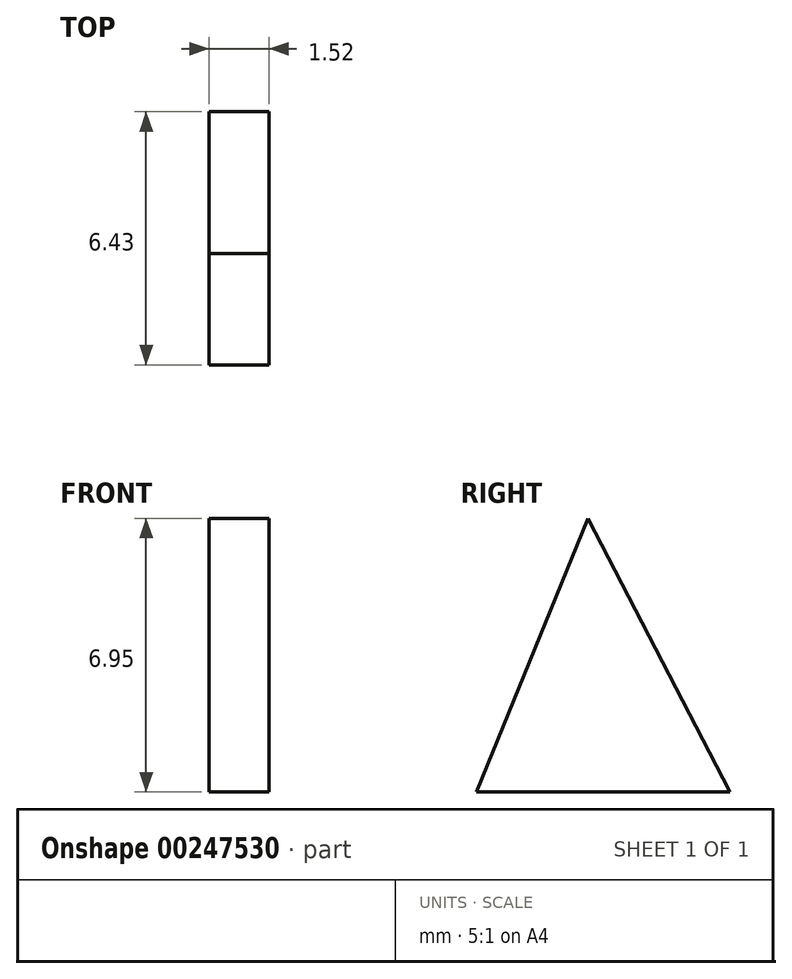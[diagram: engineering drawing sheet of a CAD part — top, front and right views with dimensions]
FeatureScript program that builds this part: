
annotation { "Feature Type Name" : "Feature", "Feature Type Description" : "" }
export const myFeature = defineFeature(function(context is Context, id is Id, definition is map)
    precondition{}
    {
        {
            var Q0;
            Q0=qCreatedBy(makeId("Right.planeOp"),FACE);
            var sketch = newSketch(context, id + "F0", { "sketchPlane" : qUnion([Q0])});
            skLineSegment(sketch, "E0", {"start": v(24.44, 31.9) * mm, "end": v(21.61, 24.95) * mm});
            skLineSegment(sketch, "E1", {"start": v(21.61, 24.95) * mm, "end": v(24.44, 31.9) * mm});
            skLineSegment(sketch, "E2", {"start": v(21.61, 24.95) * mm, "end": v(28.04, 24.95) * mm});
            skLineSegment(sketch, "E3", {"start": v(28.04, 24.95) * mm, "end": v(24.44, 31.9) * mm});
            skSolve(sketch);
        }
        {
            var Q0;
            Q0 = qSketchRegion(id + "F0", true);
            extrude(context, id + "F1", {"entities" : qUnion([Q0]), "depth" : 1.52 * mm});
        }
    });
